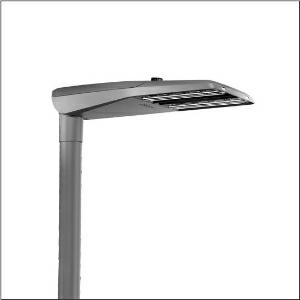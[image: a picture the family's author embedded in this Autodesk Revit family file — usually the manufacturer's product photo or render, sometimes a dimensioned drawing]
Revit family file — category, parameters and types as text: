
# Revit family: streetlight_sl_11_iq_midi___st1_2a_5xc3a41u08le_6743
name_source: partatom
category: Lighting Fixtures
units: mm (PartAtom-declared; Revit-internal decimal feet)

## family parameters
Cut with Voids When Loaded = No
Host = Face
Light Source = No
Part Type = Normal
Room Calculation Point = No
Round Connector Dimension = Use Diameter
Shared = No

## types (1)
- --- (1 x LED, 9590 lm, 59.4 W, 4000K)
    Apparent Load = 59 VA
    CIE Flux Codes = 32 70 96 100 100
    Color Rendering = 70
    Color Temperature = 4000K
    Default Elevation = 1800 mm
    Description = Streetlight SL 11 iQ midi, mast luminaire, primary light control with 3 zone facetted reflector, of plastic, silver coated, highly specular, primary optical cover: cover, of PMMA, transparent, light distribution: ST1.2a, light emission: direct distribution, primary light characteristic: asymmetric, installation type: post-top, side-entry, lamps: LED, High Power LED, rated values: 9.590lm | 59,4W | 161,4lm/W (begin service life); end service life: 9.590lm | 61,6W; at 50% lumin. flux: 4.795lm | 28,5W | 168,2lm/W, colour temperature: 4000K, colour rendering: CRI > 70, light colour: 740, light setting 1 begin service life: 100% | 9.590lm | 59,4W | 161,4lm/W | 4.000K, light setting 1 end service life: 61,6W, further light settings possible, control: pre-setting: logarithmic dimming characteristic, Street-Remote, Auto-Match, Temp-Guard, Lumen-Switch, Night-Set, Smart-Wire, Light-Fading, Desk-Remote (wireless, voltage-free reading and setting of iQ features in the workshop via application-optimized NFC function/RFID function), optimised constant luminous flux control (CLO 2.0), with cable H07RN-F 5x 1.5mm², mains connection: 230..240V, AC, 50/60Hz, connection cable pre-assembled, cable length: 8,5m, luminaire housing, of diecast aluminium, powder-coated, Siteco® metallic grey (DB 702S), please order mast flange separately, inclination adjustable without tools: 0°, 5°, 10°, 15° (post-top) | 0°, -5°, -10°, -15° (side-entry), sealing non-destructively replaceable, multi-level sealing system, length: 780mm, width: 376mm, height: 118mm, mast flange for spigot size: 42mm (side-entry): 5XC10008XM4, 60/48mm (side-entry/post-top): 5XC10108XM2, 76/60mm (side-entry/post-top): 5XC10108XM1, equipment: standard, Smart Interface below, protection rating (complete): IP66, insulation class (complete): insulation class II (safety insulation), certification: CE, ENEC, ENEC+, VDE, UKCA, impact resistance: IK10, permissible operating ambient temperature for outdoor applications: -25..+50°C, standard-compliant lighting for roads and squares, Environmental Product Declaration (EPD) tested and certified by an independent institute, packaging unit: 1 piece

Light Distribution: ST1.2a
    Height = 118 mm
    Lamp = 1 x LED
    Lamp Light Flux = 9590 lm
    Lamp Power = 59.4 W
    Lamp count = 1
    Length = 780 mm
    Luminous efficacy = 161 lm/W
    Manufacturer = Siteco
    ModVariant = No
    Model = 5XC3A41U08LE
    Number of Poles = 1
    OnlyDefault = Yes
    Power Factor = 1
    Product Name = Streetlight SL 11 iQ midi | ST1.2a
    Product group = mast luminaire | pylon top
    ProductGroupID = 6100
    Protection Class = Protection class II
    Protection Degree = IP 66
    RLX_Detail_Level = 1
    RLX_Emergency_Light_Flux = 0 lm
    RLX_Emergency_Type = 0
    RLX_Emergency_Type_DB = No
    RlxData = <blob elided: 69905 chars, md5=8efd1fd9>
    Socket = socket
    Standby Power = 0 W
    System Light Flux = 9590 lm
    System Power = 59 W
    Type Comments = factory setting: luminous flux: 100 % | dim-lin: 254 | 521 mA
    Type Image = l_1005968.jpg
    URL = http://relux.com
    VarID = @adj_133114
    Voltage = 0 V
    Weight = 0.00 kg
    Width = 376 mm

## geometry (parser evidence)
native form markers: Blend x4, Sweep x10
no freeform markers — native parametric forms only
